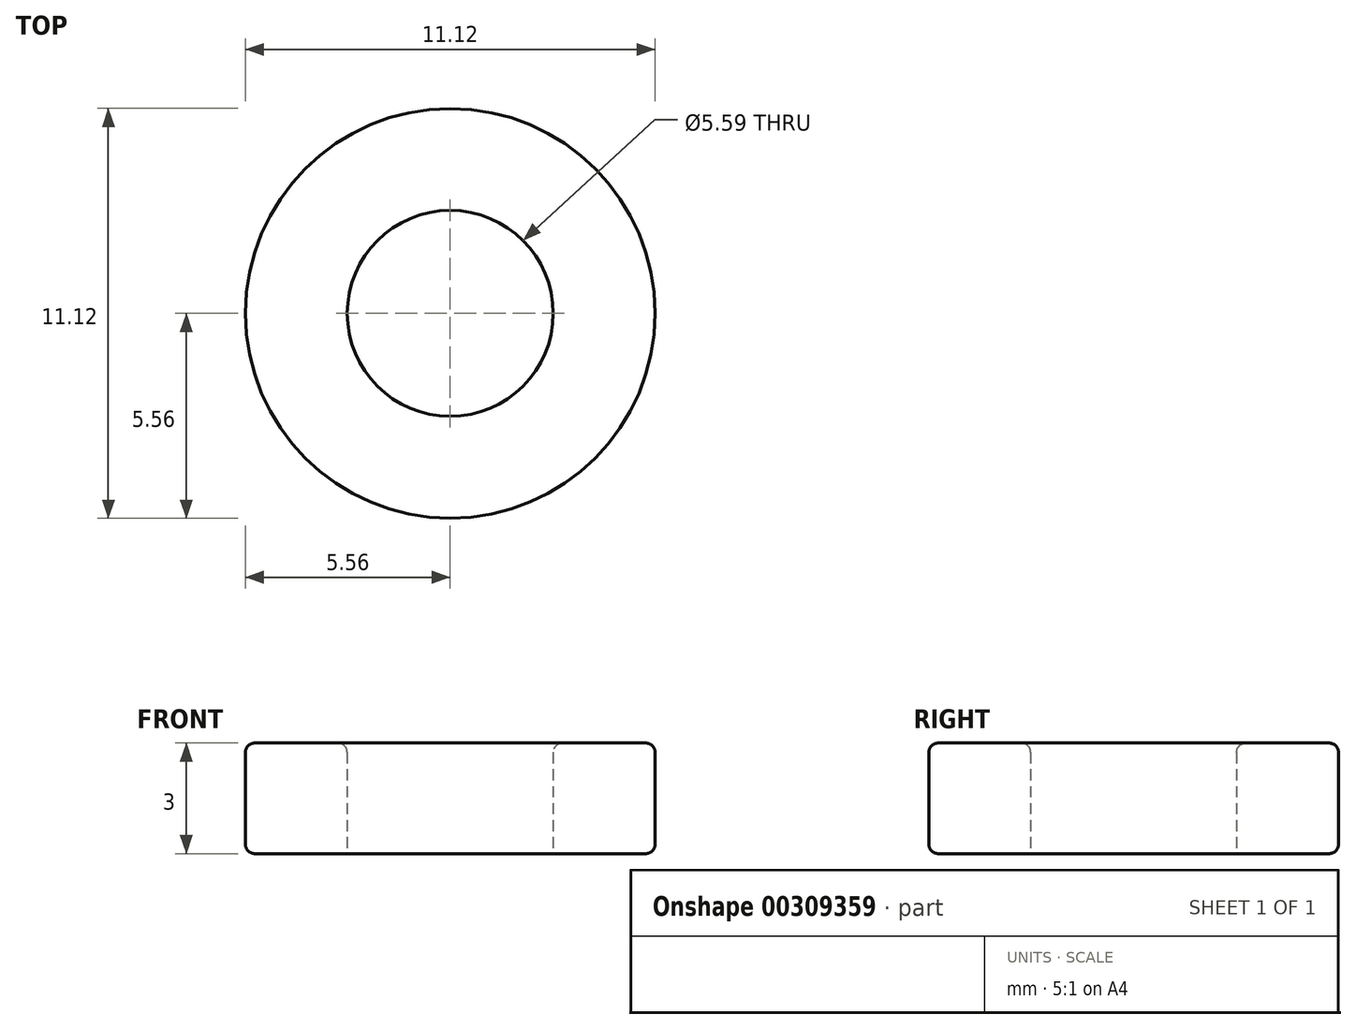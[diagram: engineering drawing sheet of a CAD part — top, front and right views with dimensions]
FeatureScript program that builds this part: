
annotation { "Feature Type Name" : "Feature", "Feature Type Description" : "" }
export const myFeature = defineFeature(function(context is Context, id is Id, definition is map)
    precondition{}
    {
        {
            var Q0;
            Q0=qCreatedBy(makeId("Top.planeOp"),FACE);
            var sketch = newSketch(context, id + "F0", { "sketchPlane" : qUnion([Q0])});
            skCircle(sketch, "E0", {"center": v(0, 0) * mm, "radius": 5.56 * mm});
            skLineSegment(sketch, "E1", {"start": v(0, 0) * mm, "end": v(5.56, 0) * mm});
            skSolve(sketch);
        }
        {
            var Q0;
            Q0 = qSketchRegion(id + "F0", true);
            extrude(context, id + "F1", {"entities" : qUnion([Q0]), "depth" : 3 * mm});
        }
        {
            var Q0;
            Q0=sQuery(id+"F0.wireOp",VERTEX,"E1.start");
            var Q1;
            Q1=makeQuery(id+"F1.opExtrude","SWEPT_BODY",BODY,{"disambiguationData":[OSD([sQuery(id+"F0.wireOp",EDGE,"E0")])]});
            hole(context, id + "F2", {"style" : HoleStyle.SIMPLE, "endStyle" : HoleEndStyle.THROUGH, "oppositeDirection" : true, "holeDiameter" : 5.6 * mm, "tappedDepth" : 12 * mm, "tapClearance" : 3, "locations" : qUnion([Q0]), "scope" : qUnion([Q1])});
        }
        {
            var Q0;
            Q0=makeQuery(id+"F1.opExtrude","CAP_EDGE",EDGE,{"disambiguationData":[OSD([sQuery(id+"F0.wireOp",EDGE,"E0")])],"isStart":true});
            var Q1;
            Q1=makeQuery(id+"F1.opExtrude","CAP_EDGE",EDGE,{"disambiguationData":[OSD([sQuery(id+"F0.wireOp",EDGE,"E0")])],"isStart":false});
            var Q2;
            Q2=makeQuery(id+"F1.opExtrude","CAP_FACE",FACE,{"disambiguationData":[OSD([sQuery(id+"F0.wireOp",EDGE,"E0")])],"isStart":false});
            var Q3;
            Q3=makeQuery(id+"F2.hole-0.boolean.opBoolean","COPY",EDGE,{"derivedFrom":makeQuery(id+"F2.hole-0.opRevolve","SWEPT_EDGE",EDGE,{"disambiguationData":[OSD([sQuery(id+"F2.hole-0.sketch.wireOp",EDGE,"core_line_2"),sQuery(id+"F2.hole-0.sketch.wireOp",EDGE,"core_line_3")])]})});
            fillet(context, id + "F3", {"entities" : qUnion([Q0, Q1, Q2, Q3]), "radius" : .25 * mm, "tangentPropagation" : true, "allowEdgeOverflow" : false});
        }
    });
